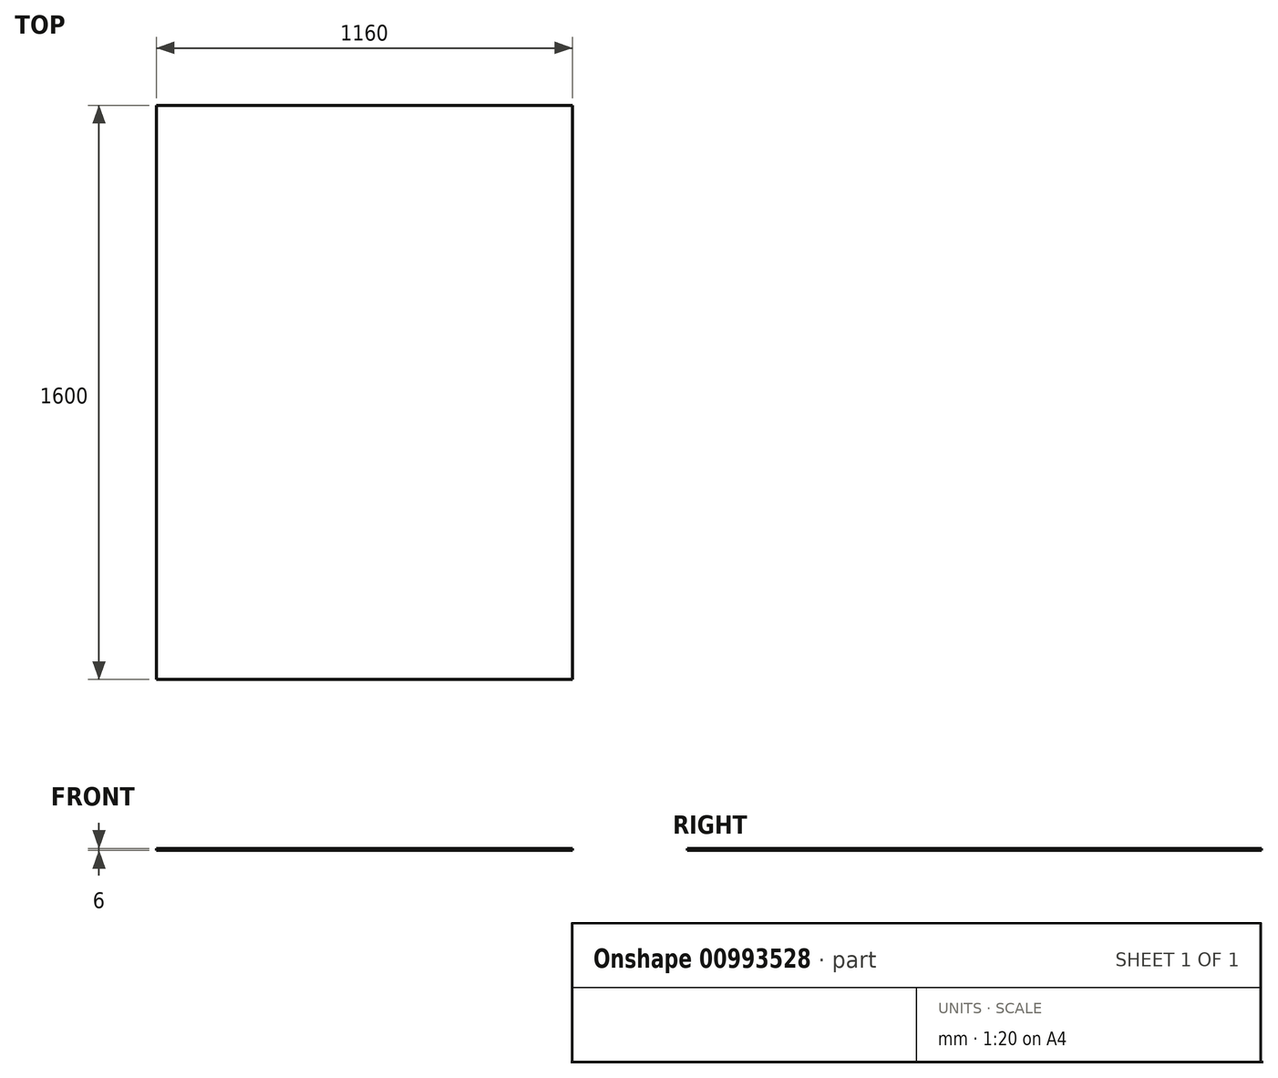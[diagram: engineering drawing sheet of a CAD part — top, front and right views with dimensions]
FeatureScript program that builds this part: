
annotation { "Feature Type Name" : "Feature", "Feature Type Description" : "" }
export const myFeature = defineFeature(function(context is Context, id is Id, definition is map)
    precondition{}
    {
        {
            var Q0;
            Q0=qCreatedBy(makeId("Top.planeOp"),FACE);
            var sketch = newSketch(context, id + "F0", { "sketchPlane" : qUnion([Q0])});
            skLineSegment(sketch, "E0.bottom", {"start": v(-582.61, 1277.28) * mm, "end": v(577.39, 1277.28) * mm});
            skLineSegment(sketch, "E0.top", {"start": v(-582.61, -322.72) * mm, "end": v(577.39, -322.72) * mm});
            skLineSegment(sketch, "E0.left", {"start": v(-582.61, 1277.28) * mm, "end": v(-582.61, -322.72) * mm});
            skLineSegment(sketch, "E0.right", {"start": v(577.39, 1277.28) * mm, "end": v(577.39, -322.72) * mm});
            skSolve(sketch);
        }
        {
            var Q0;
            Q0=makeQuery(id+"F0.imprint","IMPRINT",FACE,{"disambiguationData":[TD([[makeQuery(id+"F0.imprint","IMPRINT",EDGE,{"derivedFrom":sQuery(id+"F0.wireOp",EDGE,"E0.bottom")}),-1.0]])]});
            extrude(context, id + "F1", {"entities" : qUnion([Q0]), "endBound" : BoundingType.SYMMETRIC, "depth" : 6 * mm, "offsetDistance" : 25 * mm});
        }
    });
